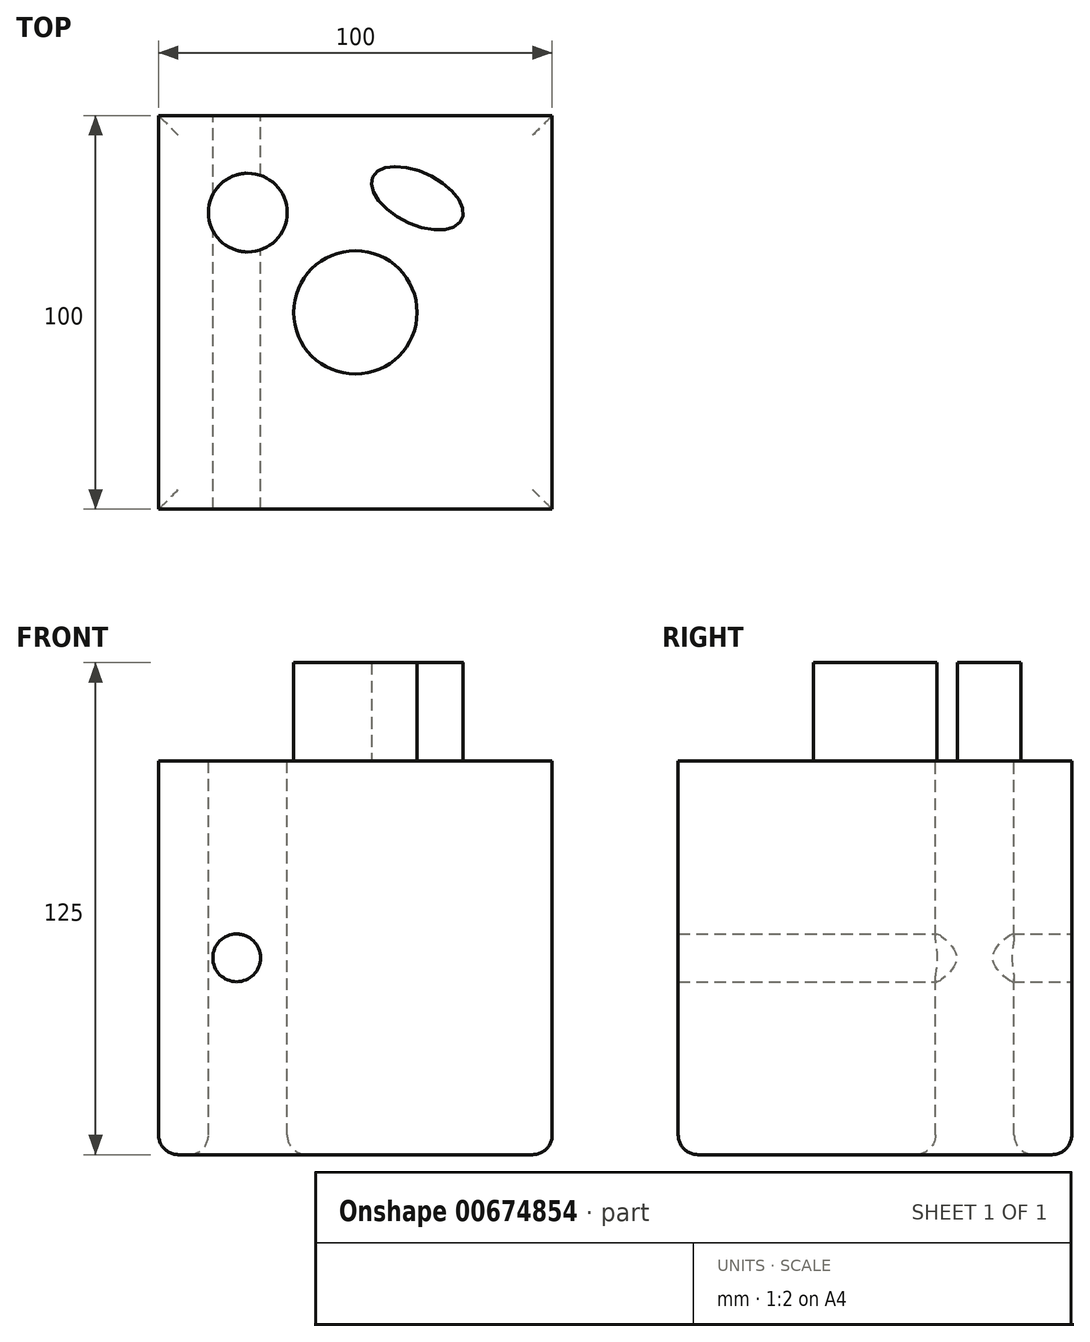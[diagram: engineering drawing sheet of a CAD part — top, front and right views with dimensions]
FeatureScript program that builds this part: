
annotation { "Feature Type Name" : "Feature", "Feature Type Description" : "" }
export const myFeature = defineFeature(function(context is Context, id is Id, definition is map)
    precondition{}
    {
        {
            var Q0;
            Q0=qCreatedBy(makeId("Front.planeOp"),FACE);
            var sketch = newSketch(context, id + "F0", { "sketchPlane" : qUnion([Q0])});
            skLineSegment(sketch, "E0.bottom", {"start": v(50, 50) * mm, "end": v(-50, 50) * mm});
            skLineSegment(sketch, "E0.top", {"start": v(50, -50) * mm, "end": v(-50, -50) * mm});
            skLineSegment(sketch, "E0.left", {"start": v(50, 50) * mm, "end": v(50, -50) * mm});
            skLineSegment(sketch, "E0.right", {"start": v(-50, 50) * mm, "end": v(-50, -50) * mm});
            skPoint(sketch, "E0.middle", {"position": v(0, 0) * mm});
            skSolve(sketch);
        }
        {
            var Q0;
            Q0=makeQuery(id+"F0.imprint","IMPRINT",FACE,{"disambiguationData":[TD([[makeQuery(id+"F0.imprint","IMPRINT",EDGE,{"derivedFrom":sQuery(id+"F0.wireOp",EDGE,"E0.bottom")}),1.0]])]});
            extrude(context, id + "F1", {"entities" : qUnion([Q0]), "endBound" : BoundingType.SYMMETRIC, "depth" : 100 * mm, "offsetDistance" : 25 * mm});
        }
        {
            var Q0;
            Q0=makeQuery(id+"F1.opExtrude","SWEPT_FACE",FACE,{"disambiguationData":[OSD([sQuery(id+"F0.wireOp",EDGE,"E0.bottom")])]});
            var sketch = newSketch(context, id + "F2", { "sketchPlane" : qUnion([Q0])});
            skCircle(sketch, "E1", {"center": v(-27.34, 25.35) * mm, "radius": 10 * mm});
            skSolve(sketch);
        }
        {
            var Q0;
            Q0=makeQuery(id+"F2.imprint","IMPRINT",FACE,{"disambiguationData":[TD([[makeQuery(id+"F2.imprint","IMPRINT",EDGE,{"derivedFrom":sQuery(id+"F2.wireOp",EDGE,"E1")}),1.0]])]});
            extrude(context, id + "F3", {"entities" : qUnion([Q0]), "operationType" : NewBodyOperationType.REMOVE, "oppositeDirection" : true, "depth" : 105 * mm, "offsetDistance" : 25 * mm});
        }
        {
            var Q0;
            Q0=makeQuery(id+"F1.opExtrude","CAP_FACE",FACE,{"disambiguationData":[OSD([sQuery(id+"F0.wireOp",EDGE,"E0.bottom"),sQuery(id+"F0.wireOp",EDGE,"E0.top"),sQuery(id+"F0.wireOp",EDGE,"E0.left"),sQuery(id+"F0.wireOp",EDGE,"E0.right")])],"isStart":true});
            var sketch = newSketch(context, id + "F4", { "sketchPlane" : qUnion([Q0])});
            skCircle(sketch, "E2", {"center": v(30.17, 0) * mm, "radius": 6.05 * mm});
            skSolve(sketch);
        }
        {
            var Q0;
            Q0=makeQuery(id+"F4.imprint","IMPRINT",FACE,{"disambiguationData":[TD([[makeQuery(id+"F4.imprint","IMPRINT",EDGE,{"derivedFrom":sQuery(id+"F4.wireOp",EDGE,"E2")}),1.0]])]});
            extrude(context, id + "F5", {"entities" : qUnion([Q0]), "operationType" : NewBodyOperationType.REMOVE, "oppositeDirection" : true, "depth" : 105 * mm, "offsetDistance" : 25 * mm});
        }
        {
            var Q0;
            Q0=makeQuery(id+"F1.opExtrude","SWEPT_FACE",FACE,{"disambiguationData":[OSD([sQuery(id+"F0.wireOp",EDGE,"E0.top")])]});
            fillet(context, id + "F6", {"entities" : qUnion([Q0]), "radius" : 5 * mm, "tangentPropagation" : true, "allowEdgeOverflow" : false});
        }
        {
            var Q0;
            Q0=makeQuery(id+"F1.opExtrude","SWEPT_FACE",FACE,{"disambiguationData":[OSD([sQuery(id+"F0.wireOp",EDGE,"E0.bottom")])]});
            var sketch = newSketch(context, id + "F7", { "sketchPlane" : qUnion([Q0])});
            skCircle(sketch, "E3", {"center": v(0, 0) * mm, "radius": 15.68 * mm});
            skSolve(sketch);
        }
        {
            var Q0;
            Q0=makeQuery(id+"F7.imprint","IMPRINT",FACE,{"disambiguationData":[TD([[makeQuery(id+"F7.imprint","IMPRINT",EDGE,{"derivedFrom":sQuery(id+"F7.wireOp",EDGE,"E3")}),1.0]])]});
            extrude(context, id + "F8", {"entities" : qUnion([Q0]), "operationType" : NewBodyOperationType.ADD, "depth" : 25 * mm, "offsetDistance" : 25 * mm});
        }
        {
            var Q0;
            Q0=makeQuery(id+"F1.opExtrude","SWEPT_FACE",FACE,{"disambiguationData":[OSD([sQuery(id+"F0.wireOp",EDGE,"E0.bottom")])]});
            var sketch = newSketch(context, id + "F9", { "sketchPlane" : qUnion([Q0])});
            skEllipse(sketch, "E4", {"center": v(15.72, 29.04) * mm, "majorRadius": 12.54 * mm, "minorRadius": 6.63 * mm, "majorAxis": v(-0.9, 0.43)});
            skSolve(sketch);
        }
        {
            var Q0;
            Q0=makeQuery(id+"F9.imprint","IMPRINT",FACE,{"disambiguationData":[TD([[makeQuery(id+"F9.imprint","IMPRINT",EDGE,{"derivedFrom":sQuery(id+"F9.wireOp",EDGE,"E4")}),1.0]])]});
            extrude(context, id + "F10", {"entities" : qUnion([Q0]), "operationType" : NewBodyOperationType.ADD, "depth" : 25 * mm, "offsetDistance" : 25 * mm});
        }
    });
